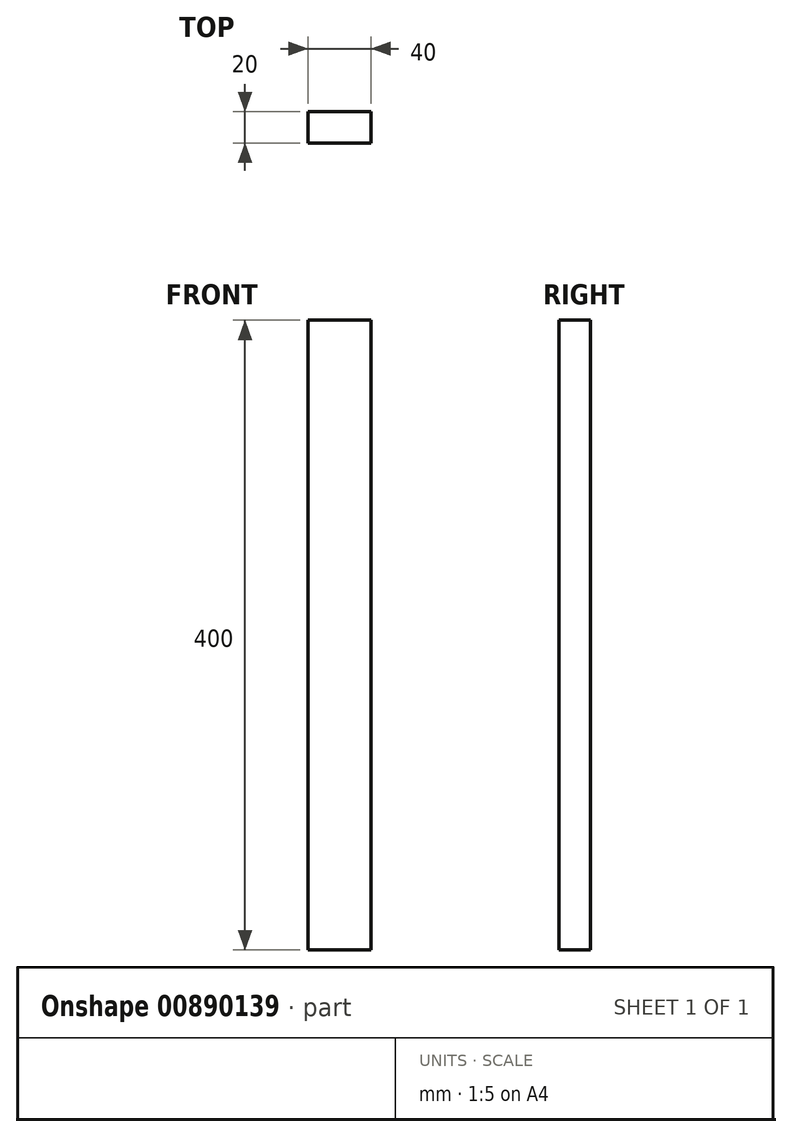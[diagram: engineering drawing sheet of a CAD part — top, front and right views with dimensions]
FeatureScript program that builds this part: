
annotation { "Feature Type Name" : "Feature", "Feature Type Description" : "" }
export const myFeature = defineFeature(function(context is Context, id is Id, definition is map)
    precondition{}
    {
        {
            var Q0;
            Q0=qCreatedBy(makeId("Front.planeOp"),FACE);
            var sketch = newSketch(context, id + "F0", { "sketchPlane" : qUnion([Q0])});
            skLineSegment(sketch, "E0", {"start": v(-20, 0) * mm, "end": v(20, 0) * mm});
            skLineSegment(sketch, "E1", {"start": v(20, 0) * mm, "end": v(20, 400) * mm});
            skLineSegment(sketch, "E2", {"start": v(20, 400) * mm, "end": v(-20, 400) * mm});
            skLineSegment(sketch, "E3", {"start": v(-20, 400) * mm, "end": v(-20, 0) * mm});
            skPoint(sketch, "E4.centerSnap0", {"position": v(0, 400) * mm});
            skSolve(sketch);
        }
        {
            var Q0;
            Q0=qSketchRegion(id+"F0",true);
            extrude(context, id + "F1", {"entities" : qUnion([Q0]), "depth" : 20 * mm, "offsetDistance" : 25 * mm});
        }
    });
